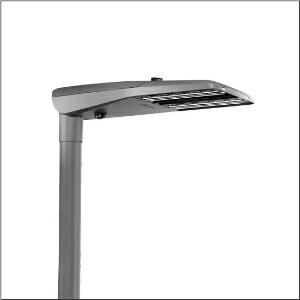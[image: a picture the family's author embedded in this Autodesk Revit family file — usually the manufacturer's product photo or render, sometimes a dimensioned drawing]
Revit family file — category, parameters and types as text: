
# Revit family: streetlight_sl_11_iq_midi___st1_2a_5xc3a51y08le_7352
name_source: partatom
category: Lighting Fixtures
units: mm (PartAtom-declared; Revit-internal decimal feet)

## family parameters
Cut with Voids When Loaded = No
Host = Face
Light Source = No
Part Type = Normal
Room Calculation Point = No
Round Connector Dimension = Use Diameter
Shared = No

## types (1)
- --- (1 x LED, 9210 lm, 59.4 W, 3000K)
    Apparent Load = 59 VA
    CIE Flux Codes = 32 70 96 100 100
    Color Rendering = 70
    Color Temperature = 3000K
    Default Elevation = 1800 mm
    Description = Streetlight SL 11 iQ midi, mast luminaire, primary light control with 3 zone facetted reflector, of plastic, silver coated, highly specular, primary optical cover: cover, of PMMA, transparent, light distribution: ST1.2a, light emission: direct distribution, primary light characteristic: asymmetric, installation type: post-top, side-entry, LED, High Power LED, rated luminous flux: 9.210lm, luminous efficacy: 155lm/W, light colour: 730, colour temperature: 3000K, control: presetting dimming logarithmic, Street-Remote, Auto-Match, Temp-Guard, Lumen-Switch, Night-Set, Smart-Wire, Light-Fading, Desk-Remote (wireless, voltage-free reading and setting of iQ features in the workshop via application-optimized NFC function/RFID function), optimised constant luminous flux control (CLO 2.0), with cable H07RN-F 5x 1.5mm², mains connection: 230..240V, AC, 50/60Hz, connection cable pre-assembled, cable length: 8,5m, start of lifetime: 59W, end of service life: 62W, reduction: 29W, luminaire housing, of diecast aluminium, powder-coated, Siteco® metallic grey (DB 702S), please order mast flange separately, inclination adjustable without tools: 0°, 5°, 10°, 15° (post-top) | 0°, -5°, -10°, -15° (side-entry), sealing non-destructively replaceable, multi-level sealing system, length: 780mm, width: 376mm, height: 118mm, mast flange for spigot size: 42mm (side-entry): 5XC10008XM4, 60/48mm (side-entry/post-top): 5XC10108XM2, 76/60mm (side-entry/post-top): 5XC10108XM1, equipment: standard, Smart Interface below and above, protection rating (complete): IP66, insulation class (complete): insulation class II (safety insulation), certification: CE, ENEC, VDE, UKCA, impact resistance: IK09, permissible operating ambient temperature for outdoor applications: -25..+50°C, standard-compliant lighting for roads and squares, Environmental Product Declaration (EPD) tested and certified by an independent institute, packaging unit: 1 piece

Light Distribution: ST1.2a
    Height = 118 mm
    Lamp = 1 x LED
    Lamp Light Flux = 9210 lm
    Lamp Power = 59.4 W
    Lamp count = 1
    Length = 780 mm
    Luminous efficacy = 155 lm/W
    Manufacturer = Siteco
    ModVariant = No
    Model = 5XC3A51Y08LE
    Number of Poles = 1
    OnlyDefault = Yes
    Power Factor = 1
    Product Name = Streetlight SL 11 iQ midi | ST1.2a
    Product group = mast luminaire | pylon top
    ProductGroupID = 6100
    Protection Class = Protection class II
    Protection Degree = IP 66
    RLX_Detail_Level = 1
    RLX_Emergency_Light_Flux = 0 lm
    RLX_Emergency_Type = 0
    RLX_Emergency_Type_DB = No
    RlxData = <blob elided: 69669 chars, md5=8ff653f3>
    Socket = socket
    Standby Power = 0 W
    System Light Flux = 9210 lm
    System Power = 59 W
    Type Comments = factory setting: luminous flux: 100 % | dim-lin: 254 | 521 mA
    Type Image = l_1004429.jpg
    URL = http://relux.com
    VarID = @adj_082681
    Voltage = 0 V
    Weight = 0.00 kg
    Width = 376 mm

## geometry (parser evidence)
native form markers: Blend x4, Sweep x9
no freeform markers — native parametric forms only
